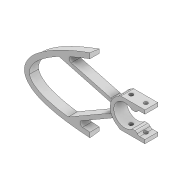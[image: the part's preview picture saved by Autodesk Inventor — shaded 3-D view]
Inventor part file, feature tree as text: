
AUTODESK INVENTOR PART (.ipt)
format: ipt  version: 2022 (Build 260153000, 153)  size: 558,592 bytes
history: native  units: mm
features: extrude x6, sketch x6, projected_geometry x3, shell x1, fillet x1, thicken_offset x1, chamfer x1
ambient origin geometry x8: Origin, YZ Plane, XZ Plane, XY Plane, X Axis, Y Axis, Z Axis, Center Point
bodies: Solid1 (feature_tree)
feature tree (19):
  extrude  "Extrusion1"  Depth=2.0mm
  shell  "Shell1"  Thickness=55.0mm
  extrude  "Extrusion9"  Depth=12.0mm
  fillet  "Fillet2"  Radius=2.0mm
  extrude  "Extrusion10"  Depth=11.0mm
  extrude  "Extrusion12"  TaperAngle=30.0deg  [1 undecoded]
  thicken_offset  "Thicken1"
  chamfer  "Chamfer1"  Distance=2.0mm
  extrude  "Extrusion13"  Depth=1.0mm
  extrude  "Extrusion14"  Depth=1.0mm
  sketch  "Sketch3"  dims[d0=5.0mm d1=0.0mm d2=2.0mm d68=55.0mm]
  sketch  "Sketch25"  dims[d69=8.05mm d70=12.0mm d71=2.0mm]
  projected_geometry  "Projected Loop13"
  sketch  "Sketch26"  dims[d72=11.0mm d73=11.0mm]
  sketch  "Sketch28"  dims[d74=15.0deg d75=30.0deg]
  sketch  "Sketch30"  dims[d76=2.0mm]
  projected_geometry  "Projected Loop15"
  sketch  "Sketch31"  dims[d77=1.0mm d79=2.0mm d80=1.0mm d81=1.5mm d82=1.5mm d83=5.0mm d84=0.0mm d85=3.0mm d86=3.0mm d87=1.5mm d88=35.0mm d89=35.0mm d90=100.0mm d91=0.0mm d98=2.1mm d99=2.5mm d100=2.1mm d101=3.0mm d102=30.0mm d103=0.0mm d104=0.7mm d105=0.7mm d106=5.0mm d107=0.65mm d108=45.0deg d109=1.0mm d110=0.0mm d111=1.0mm d112=0.0mm]
  projected_geometry  "Projected Loop16"
note: 1 required parameter value undecoded (feature->parameter linkage not recoverable at this tier; creation-order binding heuristic only, values carry confidence <= 0.55)
